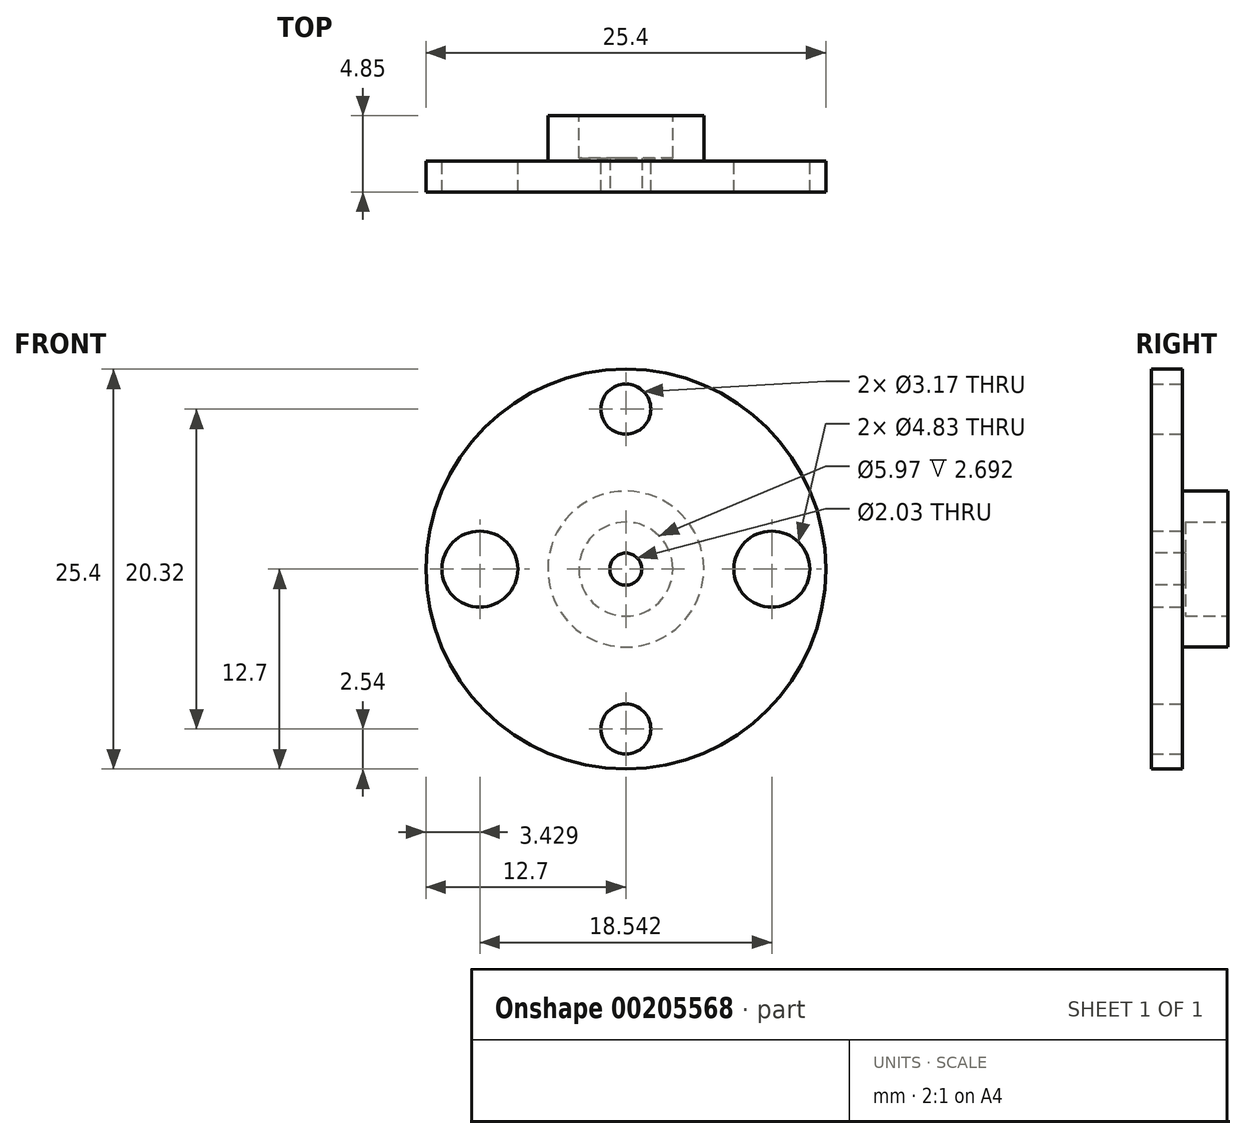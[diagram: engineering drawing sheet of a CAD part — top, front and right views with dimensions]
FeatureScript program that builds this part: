
annotation { "Feature Type Name" : "Feature", "Feature Type Description" : "" }
export const myFeature = defineFeature(function(context is Context, id is Id, definition is map)
    precondition{}
    {
        {
            var Q0;
            Q0=qCreatedBy(makeId("Front.planeOp"),FACE);
            var sketch = newSketch(context, id + "F0", { "sketchPlane" : qUnion([Q0])});
            skCircle(sketch, "E0", {"center": v(0, 0) * mm, "radius": 12.7 * mm});
            skCircle(sketch, "E1", {"center": v(0, 10.16) * mm, "radius": 1.59 * mm});
            skCircle(sketch, "E2", {"center": v(0, -10.16) * mm, "radius": 1.59 * mm});
            skCircle(sketch, "E3", {"center": v(9.27, 0) * mm, "radius": 2.41 * mm});
            skCircle(sketch, "E4", {"center": v(-9.27, 0) * mm, "radius": 2.41 * mm});
            skSolve(sketch);
        }
        {
            var Q0;
            Q0=qSketchRegion(id+"F0",true);
            extrude(context, id + "F1", {"entities" : qUnion([Q0]), "depth" : 1.98 * mm});
        }
        {
            var Q0;
            Q0=makeQuery(id+"F1.opExtrude","CAP_FACE",FACE,{"disambiguationData":[OSD([sQuery(id+"F0.wireOp",EDGE,"E0"),sQuery(id+"F0.wireOp",EDGE,"E1"),sQuery(id+"F0.wireOp",EDGE,"E2"),sQuery(id+"F0.wireOp",EDGE,"E3"),sQuery(id+"F0.wireOp",EDGE,"E4")])],"isStart":true});
            var sketch = newSketch(context, id + "F2", { "sketchPlane" : qUnion([Q0])});
            skCircle(sketch, "E5", {"center": v(0, 0) * mm, "radius": 4.95 * mm});
            skSolve(sketch);
        }
        {
            var Q0;
            Q0=qSketchRegion(id+"F2",true);
            extrude(context, id + "F3", {"entities" : qUnion([Q0]), "operationType" : NewBodyOperationType.ADD, "depth" : 2.87 * mm});
        }
        {
            var Q0;
            Q0=makeQuery(id+"F3.opExtrude","CAP_FACE",FACE,{"disambiguationData":[OSD([sQuery(id+"F2.wireOp",EDGE,"E5")])],"isStart":false});
            var sketch = newSketch(context, id + "F4", { "sketchPlane" : qUnion([Q0])});
            skCircle(sketch, "E6", {"center": v(0, 0) * mm, "radius": 2.98 * mm});
            skSolve(sketch);
        }
        {
            var Q0;
            Q0=qSketchRegion(id+"F4",true);
            extrude(context, id + "F5", {"entities" : qUnion([Q0]), "operationType" : NewBodyOperationType.REMOVE, "oppositeDirection" : true, "depth" : 2.7 * mm});
        }
        {
            var Q0;
            Q0=makeQuery(id+"F1.opExtrude","CAP_FACE",FACE,{"disambiguationData":[OSD([sQuery(id+"F0.wireOp",EDGE,"E0"),sQuery(id+"F0.wireOp",EDGE,"E1"),sQuery(id+"F0.wireOp",EDGE,"E2"),sQuery(id+"F0.wireOp",EDGE,"E3"),sQuery(id+"F0.wireOp",EDGE,"E4")])],"isStart":false});
            var sketch = newSketch(context, id + "F6", { "sketchPlane" : qUnion([Q0])});
            skCircle(sketch, "E7", {"center": v(0, 0) * mm, "radius": 1.02 * mm});
            skSolve(sketch);
        }
        {
            var Q0;
            Q0=qSketchRegion(id+"F6",true);
            extrude(context, id + "F7", {"entities" : qUnion([Q0]), "operationType" : NewBodyOperationType.REMOVE, "endBound" : BoundingType.THROUGH_ALL, "oppositeDirection" : true, "depth" : 25.4 * mm});
        }
    });
